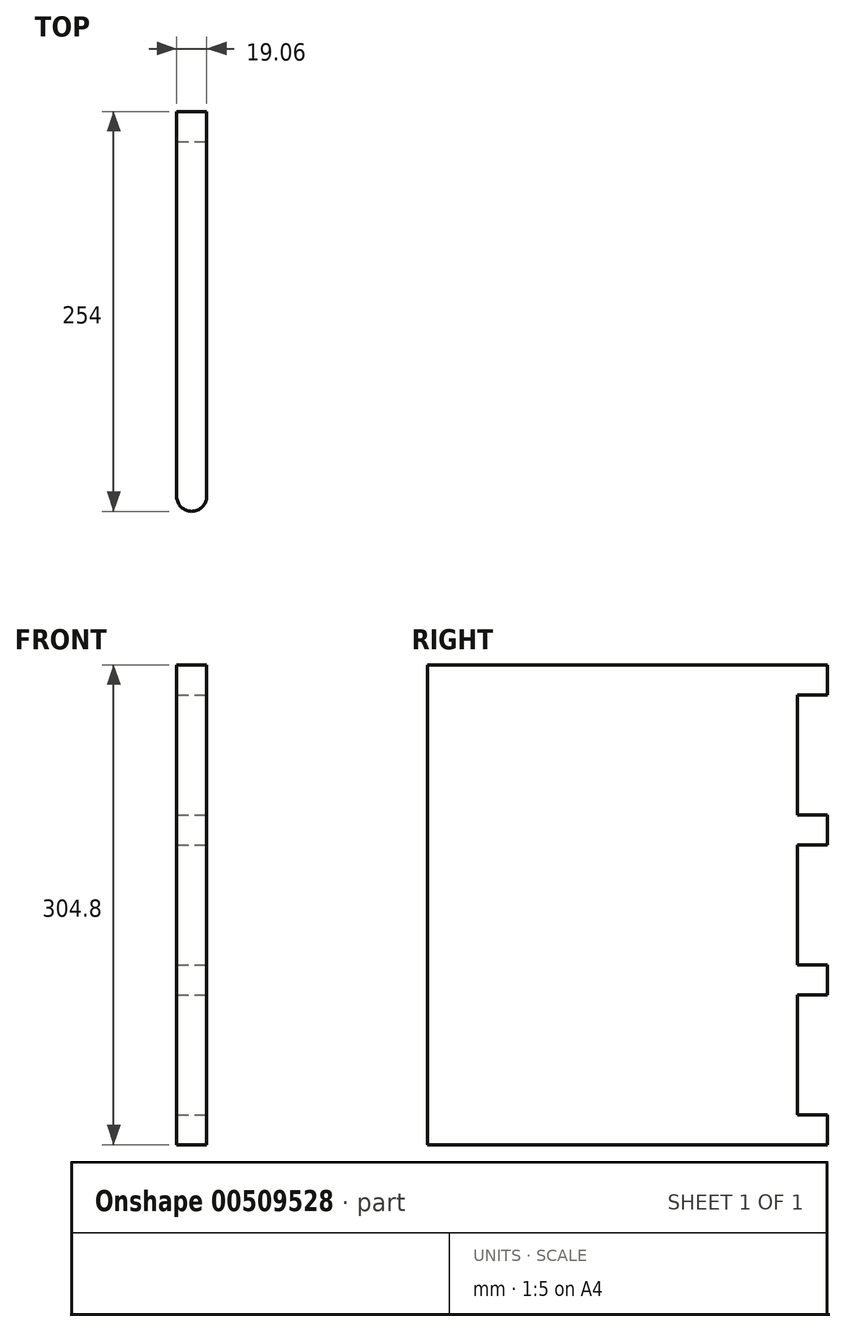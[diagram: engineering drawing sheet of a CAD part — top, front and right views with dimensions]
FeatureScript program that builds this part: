
annotation { "Feature Type Name" : "Feature", "Feature Type Description" : "" }
export const myFeature = defineFeature(function(context is Context, id is Id, definition is map)
    precondition{}
    {
        {
            var Q0;
            Q0=qCreatedBy(makeId("Right.planeOp"),FACE);
            var sketch = newSketch(context, id + "F0", { "sketchPlane" : qUnion([Q0])});
            skLineSegment(sketch, "E0.bottom", {"start": v(127, 152.4) * mm, "end": v(-127, 152.4) * mm});
            skLineSegment(sketch, "E0.top", {"start": v(127, -152.4) * mm, "end": v(-127, -152.4) * mm});
            skLineSegment(sketch, "E0.left", {"start": v(127, 152.4) * mm, "end": v(127, -152.4) * mm});
            skLineSegment(sketch, "E0.right", {"start": v(-127, 152.4) * mm, "end": v(-127, -152.4) * mm});
            skPoint(sketch, "E0.middle", {"position": v(0, 0) * mm});
            skSolve(sketch);
        }
        {
            var Q0;
            Q0=makeQuery(id+"F0.imprint","IMPRINT",FACE,{"disambiguationData":[TD([[makeQuery(id+"F0.imprint","IMPRINT",EDGE,{"derivedFrom":sQuery(id+"F0.wireOp",EDGE,"E0.bottom")}),1.0]])]});
            extrude(context, id + "F1", {"entities" : qUnion([Q0]), "endBound" : BoundingType.SYMMETRIC, "depth" : 19.05 * mm, "offsetDistance" : 25.4 * mm});
        }
        {
            var Q0;
            Q0=makeQuery(id+"F1.opExtrude","CAP_EDGE",EDGE,{"disambiguationData":[OSD([sQuery(id+"F0.wireOp",EDGE,"E0.right")])],"isStart":false});
            var Q1;
            Q1=makeQuery(id+"F1.opExtrude","CAP_EDGE",EDGE,{"disambiguationData":[OSD([sQuery(id+"F0.wireOp",EDGE,"E0.right")])],"isStart":true});
            fillet(context, id + "F2", {"entities" : qUnion([Q0, Q1]), "radius" : 9.52 * mm, "tangentPropagation" : true, "allowEdgeOverflow" : false});
        }
        {
            var Q0;
            Q0=makeQuery(id+"F1.opExtrude","CAP_FACE",FACE,{"disambiguationData":[OSD([sQuery(id+"F0.wireOp",EDGE,"E0.bottom"),sQuery(id+"F0.wireOp",EDGE,"E0.top"),sQuery(id+"F0.wireOp",EDGE,"E0.left"),sQuery(id+"F0.wireOp",EDGE,"E0.right")])],"isStart":false});
            var sketch = newSketch(context, id + "F3", { "sketchPlane" : qUnion([Q0])});
            skLineSegment(sketch, "E1", {"start": v(127, 38.1) * mm, "end": v(107.95, 38.1) * mm});
            skLineSegment(sketch, "E2", {"start": v(107.95, 38.1) * mm, "end": v(107.95, -38.1) * mm});
            skLineSegment(sketch, "E3", {"start": v(127, -38.1) * mm, "end": v(107.95, -38.1) * mm});
            skLineSegment(sketch, "E4", {"start": v(127, 38.1) * mm, "end": v(127, -38.1) * mm});
            skLineSegment(sketch, "E5", {"start": v(127, 133.35) * mm, "end": v(127, 57.15) * mm});
            skLineSegment(sketch, "E6", {"start": v(127, 57.15) * mm, "end": v(107.95, 57.15) * mm});
            skLineSegment(sketch, "E7", {"start": v(107.95, 57.15) * mm, "end": v(107.95, 133.35) * mm});
            skLineSegment(sketch, "E8", {"start": v(107.95, 133.35) * mm, "end": v(127, 133.35) * mm});
            skLineSegment(sketch, "E9", {"start": v(127, -57.15) * mm, "end": v(107.95, -57.15) * mm});
            skLineSegment(sketch, "E10", {"start": v(107.95, -57.15) * mm, "end": v(107.95, -133.35) * mm});
            skLineSegment(sketch, "E11", {"start": v(107.95, -133.35) * mm, "end": v(127, -133.35) * mm});
            skLineSegment(sketch, "E12", {"start": v(127, -133.35) * mm, "end": v(127, -57.15) * mm});
            skSolve(sketch);
        }
        {
            var Q0;
            Q0=makeQuery(id+"F3.imprint","IMPRINT",FACE,{"disambiguationData":[TD([[makeQuery(id+"F3.imprint","IMPRINT",EDGE,{"derivedFrom":sQuery(id+"F3.wireOp",EDGE,"OeNe3jhJ-xBvu-Ef8x-bsDa-piqH1Yn2xPKO")}),1.0]])]});
            var Q1;
            Q1=makeQuery(id+"F3.imprint","IMPRINT",FACE,{"disambiguationData":[TD([[makeQuery(id+"F3.imprint","IMPRINT",EDGE,{"derivedFrom":sQuery(id+"F3.wireOp",EDGE,"E5")}),-1.0]])]});
            var Q2;
            Q2=makeQuery(id+"F3.imprint","IMPRINT",FACE,{"disambiguationData":[TD([[makeQuery(id+"F3.imprint","IMPRINT",EDGE,{"derivedFrom":sQuery(id+"F3.wireOp",EDGE,"E1")}),1.0]])]});
            var Q3;
            Q3=makeQuery(id+"F3.imprint","IMPRINT",FACE,{"disambiguationData":[TD([[makeQuery(id+"F3.imprint","IMPRINT",EDGE,{"derivedFrom":sQuery(id+"F3.wireOp",EDGE,"E9")}),1.0]])]});
            var Q4;
            Q4=makeQuery(id+"F3.imprint","IMPRINT",FACE,{"disambiguationData":[TD([[makeQuery(id+"F3.imprint","IMPRINT",EDGE,{"derivedFrom":sQuery(id+"F3.wireOp",EDGE,"TS4AbZqm-4lDa-HtS0-afKt-at7Nf0DAsiyh")}),1.0]])]});
            extrude(context, id + "F4", {"entities" : qUnion([Q0, Q1, Q2, Q3, Q4]), "operationType" : NewBodyOperationType.REMOVE, "endBound" : BoundingType.THROUGH_ALL, "oppositeDirection" : true, "depth" : 25.4 * mm});
        }
    });
